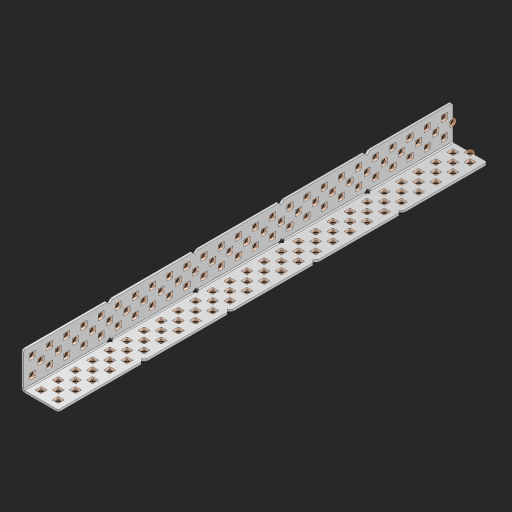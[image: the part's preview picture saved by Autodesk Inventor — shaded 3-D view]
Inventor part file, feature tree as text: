
AUTODESK INVENTOR PART (.ipt)
format: ipt  version: 2023 (Build 270158000, 158)  size: 1,796,096 bytes
history: native  units: in
note: dims shown in document units (in); Inventor stores cm internally (conversion verified against a paired STEP export)
features: other x156, extrude x148, sheet_metal_op x8, sketch x7, pattern_linear x2, mirror x1, chamfer x1
ambient origin geometry x8: Origin, YZ Plane, XZ Plane, XY Plane, X Axis, Y Axis, Z Axis, Center Point
bodies: Solid1 (feature_tree), Body (feature_tree)
feature tree (323):
  sheet_metal_op  "Flanges"
  sheet_metal_op  "Body Pattern"
  pattern_linear  "Center Pattern"  Spacing1=1.0in  [1 undecoded]
  other  "Arc Length"
  pattern_linear  "Notch Pattern"  Spacing1=0.25in  [1 undecoded]
  other  "Diagonal Plane"
  mirror  "Everything Mirrored"
  chamfer  "End Chamfer"
  sketch  "Sketch1"  dims[d0=1.0in]
  other  "Plate1"
  sketch  "Sketch2"  dims[d1=12.5in]
  other  "Plate2"
  sheet_metal_op  "Bend1"
  sheet_metal_op  "Corner1"
  sketch  "Sketch8"  dims[d2=0.0625in]
  sketch  "Sketch9"  dims[d3=0.0625in]
  other  "Srf91"
  sheet_metal_op  "Body Pattern Sketch"
  other  "Srf92"
  sketch  "Sketch13"  dims[d4=0.0312in]
  sketch  "Sketch15"  dims[d5=0.125in]
  sketch  "Sketch16"  dims[d6=0.0625in d7=1.0in d8=90.0deg d9=0.0312in d10=0.25in d11=0.0625in d12=0.0625in d49=0.182in d50=0.02in d52=0.25in d53=0.0625in d54=0.0in d55=0.172in d56=1.0in d57=0.0in d60=9.8425in d62=0.5in d63=0.7874in d65=0.5in d85=0.1473in d86=0.1782in d89=0.0625in d90=0.0in d91=0.04in d92=0.0491in d95=2.5in d96=0.04in d97=0.25in d98=45.0deg d99=0.25in d106=0.182in d107=0.02in d108=0.5in d110=0.0625in d111=0.0in d112=0.172in d113=0.5in d114=0.0in d117=0.5in d123=0.25in d125=0.25in d126=0.0491in d127=0.1473in d128=0.08in d129=0.04in d130=2.5in]
  other  "Srf786"
  other  "Srf856"
  other  "Srf857"
  other  "Srf858"
  other  "Srf859"
  other  "Srf860"
  other  "Srf861"
  other  "Srf889"
  other  "Srf890"
  other  "Srf891"
  other  "Srf1275"
  other  "Srf1276"
  other  "Srf1278"
  other  "Srf1279"
  other  "Srf1280"
  other  "Srf1281"
  other  "Srf1282"
  other  "Srf1283"
  other  "Srf1277"
  other  "Srf1285"
  other  "Srf1286"
  other  "Srf1287"
  other  "Srf1383"
  other  "Srf1384"
  other  "Srf1385"
  other  "Srf1386"
  other  "Srf1387"
  other  "Srf1388"
  other  "Srf1389"
  other  "Srf1390"
  other  "Srf1391"
  other  "Srf1392"
  other  "Srf1393"
  other  "Srf1394"
  other  "Srf1395"
  other  "Srf1396"
  other  "Srf1397"
  other  "Srf1398"
  other  "Srf1399"
  other  "Srf1400"
  other  "Srf1401"
  other  "Srf1402"
  other  "Srf1403"
  other  "Srf1404"
  other  "Srf1405"
  other  "Srf1406"
  other  "Srf1407"
  other  "Srf1408"
  other  "Srf1409"
  other  "Srf1410"
  other  "Srf1411"
  other  "Srf1412"
  other  "Srf1413"
  other  "Srf1414"
  other  "Srf1415"
  other  "Srf1416"
  other  "Srf1417"
  other  "Srf1418"
  other  "Srf1419"
  other  "Srf1420"
  other  "Srf1421"
  other  "Srf1422"
  other  "Srf1423"
  other  "Srf1424"
  other  "Srf1445"
  other  "Srf1446"
  other  "Srf1447"
  other  "Srf1448"
  other  "Srf1449"
  other  "Srf1450"
  other  "Srf1451"
  other  "Srf1452"
  other  "Srf1453"
  other  "Srf1454"
  other  "Srf1455"
  other  "Srf1456"
  other  "Srf1457"
  other  "Srf1458"
  other  "Srf1459"
  other  "Srf1460"
  other  "Srf1461"
  other  "Srf1462"
  other  "Srf1463"
  other  "Srf1464"
  other  "Srf1465"
  other  "Srf1475"
  other  "Srf1476"
  other  "Srf1477"
  other  "Srf1478"
  other  "Srf1479"
  other  "Srf1480"
  other  "Srf1481"
  other  "Srf1482"
  other  "Srf1483"
  other  "Srf1484"
  other  "Srf1485"
  other  "Srf1486"
  other  "Srf1487"
  other  "Srf1488"
  other  "Srf1489"
  other  "Srf1490"
  other  "Srf1491"
  other  "Srf1492"
  other  "Srf1493"
  other  "Srf1494"
  other  "Srf1495"
  other  "Srf1496"
  other  "Srf1497"
  other  "Srf1498"
  other  "Srf1499"
  other  "Srf1500"
  other  "Srf1501"
  other  "Srf1502"
  other  "Srf1503"
  other  "Srf1504"
  other  "Srf1505"
  other  "Srf1506"
  other  "Srf1507"
  other  "Srf1508"
  other  "Srf1509"
  other  "Srf1510"
  other  "Srf1511"
  other  "Srf1512"
  other  "Srf1513"
  other  "Srf1514"
  other  "Srf1515"
  other  "Srf1516"
  other  "Srf1537"
  other  "Srf1538"
  other  "Srf1539"
  other  "Srf1540"
  other  "Srf1541"
  other  "Srf1542"
  other  "Srf1543"
  other  "Srf1544"
  other  "Srf1545"
  other  "Srf1546"
  other  "Srf1547"
  other  "Srf1548"
  other  "Srf1549"
  other  "Srf1550"
  other  "Srf1551"
  other  "Srf1552"
  other  "Srf1553"
  other  "Srf1554"
  other  "Srf1555"
  other  "Srf1556"
  other  "Srf1557"
  sheet_metal_op  "Body Stamp"
  sheet_metal_op  "Body Circle"
  other  "Center Stamp"
  other  "Center Circle"
  sheet_metal_op  "Notch"
  extrude  "ExtrusionSrf92"  Depth=0.0625in
  extrude  "ExtrusionSrf856"  Depth=0.0625in
  extrude  "ExtrusionSrf857"  Depth=0.182in
  extrude  "ExtrusionSrf858"  Depth=0.02in
  extrude  "ExtrusionSrf859"  Depth=0.25in
  extrude  "ExtrusionSrf860"  Depth=0.0625in
  extrude  "ExtrusionSrf861"  TaperAngle=0.0deg  [1 undecoded]
  extrude  "ExtrusionSrf889"  Depth=2.5in
  extrude  "ExtrusionSrf890"  Depth=1.0in TaperAngle=0.0deg
  extrude  "ExtrusionSrf891"  Depth=2.5in
  extrude  "ExtrusionSrf1275"  Depth=0.5in
  extrude  "ExtrusionSrf1276"  Depth=2.5in
  extrude  "ExtrusionSrf1277"  Depth=2.5in
  extrude  "ExtrusionSrf1278"  Depth=0.0625in
  extrude  "ExtrusionSrf1279"  Depth=2.5in TaperAngle=0.0deg
  extrude  "ExtrusionSrf1280"  Depth=2.5in
  extrude  "ExtrusionSrf1281"  Depth=0.25in TaperAngle=45.0deg
  extrude  "ExtrusionSrf1282"  Depth=0.25in
  extrude  "ExtrusionSrf1345"  Depth=0.182in
  extrude  "ExtrusionSrf1346"  Depth=0.02in
  extrude  "ExtrusionSrf1347"  Depth=0.5in
  extrude  "ExtrusionSrf1348"  Depth=0.0625in
  extrude  "ExtrusionSrf1383"  TaperAngle=0.0deg  [1 undecoded]
  extrude  "ExtrusionSrf1384"  Depth=2.5in
  extrude  "ExtrusionSrf1385"  Depth=0.5in TaperAngle=0.0deg
  extrude  "ExtrusionSrf1386"  Depth=0.5in
  extrude  "ExtrusionSrf1387"  Depth=0.25in
  extrude  "ExtrusionSrf1388"  Depth=0.25in
  extrude  "ExtrusionSrf1389"  Depth=2.5in
  extrude  "ExtrusionSrf1390"  Depth=2.5in
  extrude  "ExtrusionSrf1391"  Depth=2.5in
  extrude  "ExtrusionSrf1392"  Depth=2.5in
  extrude  "ExtrusionSrf1393"  Depth=2.5in
  extrude  "ExtrusionSrf1394"  [1 undecoded]
  extrude  "ExtrusionSrf1395"  [1 undecoded]
  extrude  "ExtrusionSrf1396"  [1 undecoded]
  extrude  "ExtrusionSrf1397"  [1 undecoded]
  extrude  "ExtrusionSrf1398"  [1 undecoded]
  extrude  "ExtrusionSrf1399"  [1 undecoded]
  extrude  "ExtrusionSrf1400"  [1 undecoded]
  extrude  "ExtrusionSrf1401"  [1 undecoded]
  extrude  "ExtrusionSrf1402"  [1 undecoded]
  extrude  "ExtrusionSrf1403"  [1 undecoded]
  extrude  "ExtrusionSrf1404"  [1 undecoded]
  extrude  "ExtrusionSrf1405"  [1 undecoded]
  extrude  "ExtrusionSrf1406"  [1 undecoded]
  extrude  "ExtrusionSrf1407"  [1 undecoded]
  extrude  "ExtrusionSrf1408"  [1 undecoded]
  extrude  "ExtrusionSrf1409"  [1 undecoded]
  extrude  "ExtrusionSrf1410"  [1 undecoded]
  extrude  "ExtrusionSrf1411"  [1 undecoded]
  extrude  "ExtrusionSrf1412"  [1 undecoded]
  extrude  "ExtrusionSrf1413"  [1 undecoded]
  extrude  "ExtrusionSrf1414"  [1 undecoded]
  extrude  "ExtrusionSrf1415"  [1 undecoded]
  extrude  "ExtrusionSrf1416"  [1 undecoded]
  extrude  "ExtrusionSrf1417"  [1 undecoded]
  extrude  "ExtrusionSrf1418"  [1 undecoded]
  extrude  "ExtrusionSrf1419"  [1 undecoded]
  extrude  "ExtrusionSrf1420"  [1 undecoded]
  extrude  "ExtrusionSrf1421"  [1 undecoded]
  extrude  "ExtrusionSrf1422"  [1 undecoded]
  extrude  "ExtrusionSrf1423"  [1 undecoded]
  extrude  "ExtrusionSrf1424"  [1 undecoded]
  extrude  "ExtrusionSrf1445"  [1 undecoded]
  extrude  "ExtrusionSrf1446"  [1 undecoded]
  extrude  "ExtrusionSrf1447"  [1 undecoded]
  extrude  "ExtrusionSrf1448"  [1 undecoded]
  extrude  "ExtrusionSrf1449"  [1 undecoded]
  extrude  "ExtrusionSrf1450"  [1 undecoded]
  extrude  "ExtrusionSrf1451"  [1 undecoded]
  extrude  "ExtrusionSrf1452"  [1 undecoded]
  extrude  "ExtrusionSrf1453"  [1 undecoded]
  extrude  "ExtrusionSrf1454"  [1 undecoded]
  extrude  "ExtrusionSrf1455"  [1 undecoded]
  extrude  "ExtrusionSrf1456"  [1 undecoded]
  extrude  "ExtrusionSrf1457"  [1 undecoded]
  extrude  "ExtrusionSrf1458"  [1 undecoded]
  extrude  "ExtrusionSrf1459"  [1 undecoded]
  extrude  "ExtrusionSrf1460"  [1 undecoded]
  extrude  "ExtrusionSrf1461"  [1 undecoded]
  extrude  "ExtrusionSrf1462"  [1 undecoded]
  extrude  "ExtrusionSrf1463"  [1 undecoded]
  extrude  "ExtrusionSrf1464"  [1 undecoded]
  extrude  "ExtrusionSrf1465"  [1 undecoded]
  extrude  "ExtrusionSrf1475"  [1 undecoded]
  extrude  "ExtrusionSrf1476"  [1 undecoded]
  extrude  "ExtrusionSrf1477"  [1 undecoded]
  extrude  "ExtrusionSrf1478"  [1 undecoded]
  extrude  "ExtrusionSrf1479"  [1 undecoded]
  extrude  "ExtrusionSrf1480"  [1 undecoded]
  extrude  "ExtrusionSrf1481"  [1 undecoded]
  extrude  "ExtrusionSrf1482"  [1 undecoded]
  extrude  "ExtrusionSrf1483"  [1 undecoded]
  extrude  "ExtrusionSrf1484"  [1 undecoded]
  extrude  "ExtrusionSrf1485"  [1 undecoded]
  extrude  "ExtrusionSrf1486"  [1 undecoded]
  extrude  "ExtrusionSrf1487"  [1 undecoded]
  extrude  "ExtrusionSrf1488"  [1 undecoded]
  extrude  "ExtrusionSrf1489"  [1 undecoded]
  extrude  "ExtrusionSrf1490"  [1 undecoded]
  extrude  "ExtrusionSrf1491"  [1 undecoded]
  extrude  "ExtrusionSrf1492"  [1 undecoded]
  extrude  "ExtrusionSrf1493"  [1 undecoded]
  extrude  "ExtrusionSrf1494"  [1 undecoded]
  extrude  "ExtrusionSrf1495"  [1 undecoded]
  extrude  "ExtrusionSrf1496"  [1 undecoded]
  extrude  "ExtrusionSrf1497"  [1 undecoded]
  extrude  "ExtrusionSrf1498"  [1 undecoded]
  extrude  "ExtrusionSrf1499"  [1 undecoded]
  extrude  "ExtrusionSrf1500"  [1 undecoded]
  extrude  "ExtrusionSrf1501"  [1 undecoded]
  extrude  "ExtrusionSrf1502"  [1 undecoded]
  extrude  "ExtrusionSrf1503"  [1 undecoded]
  extrude  "ExtrusionSrf1504"  [1 undecoded]
  extrude  "ExtrusionSrf1505"  [1 undecoded]
  extrude  "ExtrusionSrf1506"  [1 undecoded]
  extrude  "ExtrusionSrf1507"  [1 undecoded]
  extrude  "ExtrusionSrf1508"  [1 undecoded]
  extrude  "ExtrusionSrf1509"  [1 undecoded]
  extrude  "ExtrusionSrf1510"  [1 undecoded]
  extrude  "ExtrusionSrf1511"  [1 undecoded]
  extrude  "ExtrusionSrf1512"  [1 undecoded]
  extrude  "ExtrusionSrf1513"  [1 undecoded]
  extrude  "ExtrusionSrf1514"  [1 undecoded]
  extrude  "ExtrusionSrf1515"  [1 undecoded]
  extrude  "ExtrusionSrf1516"  [1 undecoded]
  extrude  "ExtrusionSrf1537"  [1 undecoded]
  extrude  "ExtrusionSrf1538"  [1 undecoded]
  extrude  "ExtrusionSrf1539"  [1 undecoded]
  extrude  "ExtrusionSrf1540"  [1 undecoded]
  extrude  "ExtrusionSrf1541"  [1 undecoded]
  extrude  "ExtrusionSrf1542"  [1 undecoded]
  extrude  "ExtrusionSrf1543"  [1 undecoded]
  extrude  "ExtrusionSrf1544"  [1 undecoded]
  extrude  "ExtrusionSrf1545"  [1 undecoded]
  extrude  "ExtrusionSrf1546"  [1 undecoded]
  extrude  "ExtrusionSrf1547"  [1 undecoded]
  extrude  "ExtrusionSrf1548"  [1 undecoded]
  extrude  "ExtrusionSrf1549"  [1 undecoded]
  extrude  "ExtrusionSrf1550"  [1 undecoded]
  extrude  "ExtrusionSrf1551"  [1 undecoded]
  extrude  "ExtrusionSrf1552"  [1 undecoded]
  extrude  "ExtrusionSrf1553"  [1 undecoded]
  extrude  "ExtrusionSrf1554"  [1 undecoded]
  extrude  "ExtrusionSrf1555"  [1 undecoded]
  extrude  "ExtrusionSrf1556"  [1 undecoded]
  extrude  "ExtrusionSrf1557"  [1 undecoded]
note: 119 required parameter values undecoded (feature->parameter linkage not recoverable at this tier; creation-order binding heuristic only, values carry confidence <= 0.55)
